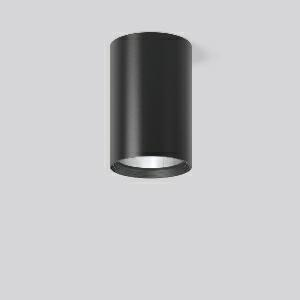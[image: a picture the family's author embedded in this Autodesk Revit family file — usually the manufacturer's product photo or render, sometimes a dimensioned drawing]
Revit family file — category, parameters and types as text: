
# Revit family: heledon_maxi_a_931244_003_2_76_fe7d
name_source: partatom
category: Lighting Fixtures
units: mm (PartAtom-declared; Revit-internal decimal feet)

## family parameters
Cut with Voids When Loaded = No
Host = Face
Light Source = No
Part Type = Normal
Room Calculation Point = No
Round Connector Dimension = Use Diameter
Shared = No

## types (1)
- HELEDON maxi A (1 x LED Modul 927 bakery, 3300 lm, 2700)
    Apparent Load = 33 VA
    Approval mark = CE
    CIE Flux Codes = 100 100 100 100 100
    Color Rendering = 90
    Color Temperature = 2700
    Default Elevation = 1800 mm
    Description = Series: HELEDON maxi
Cylindrical surface-mounted downlight. Housing: die-cast aluminium, powder-coated. Internal ceiling frame polycarbonate with bayonet mounting. Black plastic ring and recessed LED to prevent glare from the side. Optical assembly with reflector made of MIRO-Silver with 98% total light reflection for outstanding efficiency - can be changed without tools. Special LED for illumination of pastries included. Suitable for Ceiling mounting. Easy installation with a separate ceiling frame with bayonet mounting and plug connection. Driver integrated. Connected via plug-in connector. High quality converter without flickering and stroboscopic effect. The following accessories can be mounted without use of tools: interchangeable lenses, decorative glasses, honeycomb louvre, clear and frosted diffusers, white interchangeable plastic ring. 
Colour: deep black, matt (RAL 9005)
Diameter: 123 mm
Height: 183 mm
Lamp: LED
Socket: without socket
Colour temperature: bakery
Colour rendering index (CRI): 97
System power: 33 W
Rated luminous flux: 3300 lm
Luminous efficiency: 100 lm/W
Control gear: Converter, dimmable, DALI
Protection class: I
Type of protection: IP 20
    Height = 183 mm
    Lamp = 1 x LED Modul 927 bakery
    Lamp Light Flux = 3300 lm
    Lamp count = 1
    Length = 123 mm
    Lifetime = 50000 h
    Luminous efficacy = 100 lm/W
    Manufacturer = RZB
    ModVariant = No
    Model = 931244.003.2.76
    Mounting Place = Ceiling
    Mounting Type = Surface mounted
    Number of Poles = 1
    OnlyDefault = Yes
    Power Factor = 1
    Product Name = HELEDON maxi A
    Product group = Surface mounted downlights
    ProductGroupID = 302
    Protection Class = Protection class I
    Protection Degree = IP 20
    RLX_Detail_Level = 1
    RLX_Emergency_Light_Flux = 0 lm
    RLX_Emergency_Type = 0
    RLX_Emergency_Type_DB = No
    RlxData = <blob elided: 97137 chars, md5=a9594073>
    Socket = socket
    Standby Power = 0 W
    System Light Flux = 3300 lm
    System Power = 33 W
    Type Comments = Product without accessories
    Type Image = 931192.003.jpg
    URL = http://relux.com
    VarID = ---
    Voltage = 230 V
    Voltage Range = 220-240 V
    Weight = 0.00 kg
    Width = 0 mm  [stored 0 ft]

note: [stored X ft] marks values corroborated as IEEE doubles in the binary element streams (Revit-internal decimal feet)

## geometry (parser evidence)
native form markers: Blend x4, Sweep x10
no freeform markers — native parametric forms only
